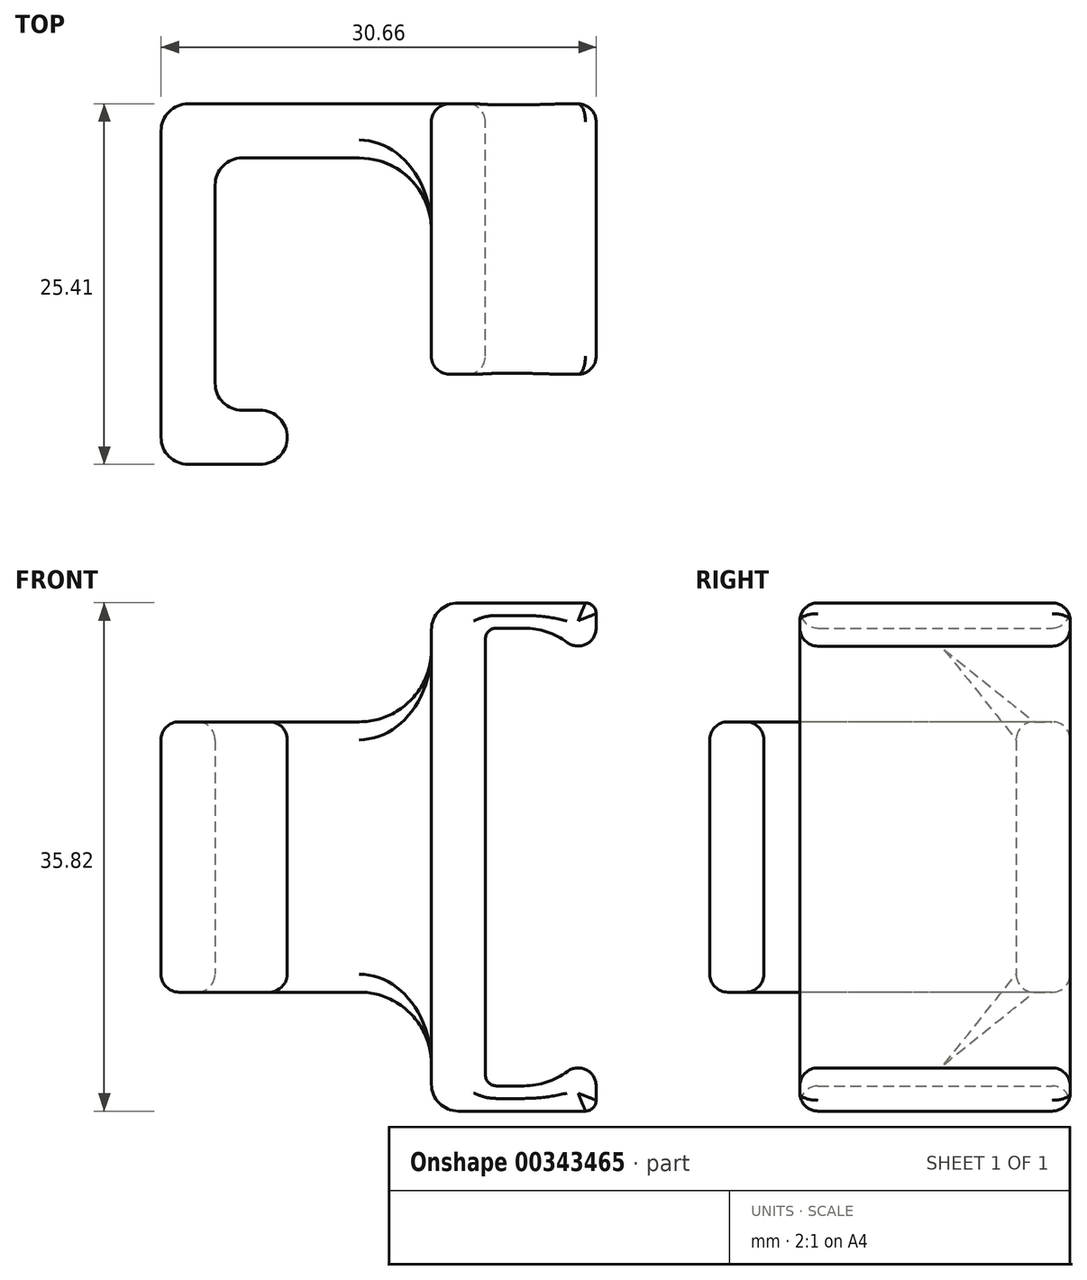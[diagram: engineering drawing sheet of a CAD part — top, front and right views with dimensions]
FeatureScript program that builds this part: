
annotation { "Feature Type Name" : "Feature", "Feature Type Description" : "" }
export const myFeature = defineFeature(function(context is Context, id is Id, definition is map)
    precondition{}
    {
        {
            var Q0;
            Q0=qCreatedBy(makeId("Front.planeOp"),FACE);
            var sketch = newSketch(context, id + "F0", { "sketchPlane" : qUnion([Q0])});
            skLineSegment(sketch, "E0.top", {"start": v(1.9, 17.9) * mm, "end": v(3.8, 17.9) * mm});
            skLineSegment(sketch, "E0.left", {"start": v(0, -16) * mm, "end": v(0, 16) * mm});
            skLineSegment(sketch, "E0.right", {"start": v(3.8, -15.37) * mm, "end": v(3.8, 15.37) * mm});
            skLineSegment(sketch, "E1", {"start": v(4.57, 16.13) * mm, "end": v(9.07, 16.13) * mm});
            skLineSegment(sketch, "E2", {"start": v(4.57, -16.13) * mm, "end": v(9.07, -16.13) * mm});
            skLineSegment(sketch, "E3", {"start": v(1.9, -17.9) * mm, "end": v(10.85, -17.9) * mm});
            skLineSegment(sketch, "E4", {"start": v(3.8, 17.9) * mm, "end": v(10.85, 17.9) * mm});
            skLineSegment(sketch, "E5.trimOffspring", {"start": v(3.8, 17.9) * mm, "end": v(3.8, 17.9) * mm});
            skLineSegment(sketch, "E6", {"start": v(11.6, -16.13) * mm, "end": v(11.6, -17.14) * mm});
            skLineSegment(sketch, "E7", {"start": v(11.6, 16.13) * mm, "end": v(11.6, 17.14) * mm});
            skPoint(sketch, "E8.visualSharp", {"position": v(0, -17.9) * mm});
            skArc(sketch, "E8.filletArc", {"start": v(0, -16) * mm, "mid": v(0.56, -17.35) * mm, "end": v(1.9, -17.9) * mm});
            skPoint(sketch, "E9.visualSharp", {"position": v(3.8, -16.13) * mm});
            skArc(sketch, "E9.filletArc", {"start": v(3.8, -15.37) * mm, "mid": v(4.03, -15.9) * mm, "end": v(4.57, -16.13) * mm});
            skPoint(sketch, "E10.visualSharp", {"position": v(3.8, 16.13) * mm});
            skArc(sketch, "E10.filletArc", {"start": v(4.57, 16.13) * mm, "mid": v(4.03, 15.9) * mm, "end": v(3.8, 15.37) * mm});
            skPoint(sketch, "E11.visualSharp", {"position": v(11.6, 17.9) * mm});
            skArc(sketch, "E11.filletArc", {"start": v(11.6, 17.14) * mm, "mid": v(11.38, 17.68) * mm, "end": v(10.85, 17.9) * mm});
            skPoint(sketch, "E12.visualSharp", {"position": v(11.6, -17.9) * mm});
            skArc(sketch, "E12.filletArc", {"start": v(10.85, -17.9) * mm, "mid": v(11.38, -17.68) * mm, "end": v(11.6, -17.14) * mm});
            skLineSegment(sketch, "E13", {"start": v(11.6, 16.13) * mm, "end": v(9.07, 16.13) * mm, "construction": true});
            skArc(sketch, "E14", {"start": v(11.6, 16.13) * mm, "mid": v(10.34, 14.86) * mm, "end": v(9.07, 16.13) * mm});
            skLineSegment(sketch, "E15", {"start": v(11.6, -16.13) * mm, "end": v(9.07, -16.13) * mm, "construction": true});
            skArc(sketch, "E16", {"start": v(11.6, -16.13) * mm, "mid": v(10.34, -14.86) * mm, "end": v(9.07, -16.13) * mm});
            skPoint(sketch, "E17.visualSharp", {"position": v(0, 17.9) * mm});
            skArc(sketch, "E17.filletArc", {"start": v(1.9, 17.9) * mm, "mid": v(0.56, 17.35) * mm, "end": v(0, 16) * mm});
            skSolve(sketch);
        }
        {
            var Q0;
            Q0 = qSketchRegion(id + "F0", true);
            extrude(context, id + "F1", {"entities" : qUnion([Q0]), "endBound" : BoundingType.SYMMETRIC, "depth" : 19.05 * mm});
        }
        {
            var Q0;
            Q0=qCreatedBy(makeId("Top.planeOp"),FACE);
            var sketch = newSketch(context, id + "F2", { "sketchPlane" : qUnion([Q0])});
            skLineSegment(sketch, "E18", {"start": v(1.9, 9.53) * mm, "end": v(-17.14, 9.52) * mm});
            skLineSegment(sketch, "E19", {"start": v(-19.05, 7.62) * mm, "end": v(-19.05, -13.97) * mm});
            skLineSegment(sketch, "E20", {"start": v(-15.24, 3.8) * mm, "end": v(-15.24, -10.16) * mm});
            skLineSegment(sketch, "E21", {"start": v(-15.24, -15.88) * mm, "end": v(-17.14, -15.88) * mm});
            skLineSegment(sketch, "E22", {"start": v(-13.33, 5.71) * mm, "end": v(1.9, 5.71) * mm});
            skLineSegment(sketch, "E23", {"start": v(-15.24, -15.88) * mm, "end": v(-12.07, -15.88) * mm});
            skLineSegment(sketch, "E24", {"start": v(-10.16, -13.97) * mm, "end": v(-10.16, -13.97) * mm});
            skLineSegment(sketch, "E25", {"start": v(-12.07, -12.07) * mm, "end": v(-13.33, -12.07) * mm});
            skPoint(sketch, "E26.visualSharp", {"position": v(-15.24, -12.07) * mm});
            skArc(sketch, "E26.filletArc", {"start": v(-15.24, -10.16) * mm, "mid": v(-14.68, -11.5) * mm, "end": v(-13.33, -12.07) * mm});
            skPoint(sketch, "E27.visualSharp", {"position": v(-19.05, -15.88) * mm});
            skArc(sketch, "E27.filletArc", {"start": v(-19.05, -13.97) * mm, "mid": v(-18.5, -15.32) * mm, "end": v(-17.14, -15.88) * mm});
            skPoint(sketch, "E28.visualSharp", {"position": v(-19.05, 9.52) * mm});
            skArc(sketch, "E28.filletArc", {"start": v(-17.14, 9.52) * mm, "mid": v(-18.5, 8.97) * mm, "end": v(-19.05, 7.62) * mm});
            skPoint(sketch, "E29.visualSharp", {"position": v(-15.24, 5.71) * mm});
            skArc(sketch, "E29.filletArc", {"start": v(-13.33, 5.72) * mm, "mid": v(-14.68, 5.16) * mm, "end": v(-15.24, 3.8) * mm});
            skPoint(sketch, "E30.visualSharp", {"position": v(-10.16, -12.07) * mm});
            skArc(sketch, "E30.filletArc", {"start": v(-10.16, -13.97) * mm, "mid": v(-10.72, -12.62) * mm, "end": v(-12.07, -12.07) * mm});
            skPoint(sketch, "E31.visualSharp", {"position": v(-10.16, -15.88) * mm});
            skArc(sketch, "E31.filletArc", {"start": v(-12.07, -15.88) * mm, "mid": v(-10.72, -15.32) * mm, "end": v(-10.16, -13.97) * mm});
            skLineSegment(sketch, "E32", {"start": v(1.9, 9.53) * mm, "end": v(1.9, 5.71) * mm});
            skPoint(sketch, "E33.orphan", {"position": v(1.26, 5.71) * mm});
            skSolve(sketch);
        }
        {
            var Q0;
            Q0 = qSketchRegion(id + "F2", true);
            extrude(context, id + "F3", {"entities" : qUnion([Q0]), "operationType" : NewBodyOperationType.ADD, "endBound" : BoundingType.SYMMETRIC, "depth" : 19.05 * mm});
        }
        {
            var Q0;
            Q0=makeQuery(id+"F1.opExtrude","SWEPT_EDGE",EDGE,{"disambiguationData":[OSD([sQuery(id+"F0.wireOp",EDGE,"E1"),sQuery(id+"F0.wireOp",EDGE,"E14")])]});
            var Q1;
            Q1=makeQuery(id+"F1.opExtrude","SWEPT_EDGE",EDGE,{"disambiguationData":[OSD([sQuery(id+"F0.wireOp",EDGE,"E2"),sQuery(id+"F0.wireOp",EDGE,"E16")])]});
            var Q2;
            Q2=makeQuery(id+"F3.boolean.opBoolean","INTERSECT",EDGE,{"derivedFrom":[makeQuery(id+"F1.opExtrude","SWEPT_FACE",FACE,{"disambiguationData":[OSD([sQuery(id+"F0.wireOp",EDGE,"E0.left")])]}),makeQuery(id+"F3.opExtrude","SWEPT_FACE",FACE,{"disambiguationData":[OSD([sQuery(id+"F2.wireOp",EDGE,"E22")])]})]});
            var Q3;
            Q3=makeQuery(id+"F3.boolean.opBoolean","INTERSECT",EDGE,{"derivedFrom":[makeQuery(id+"F1.opExtrude","SWEPT_FACE",FACE,{"disambiguationData":[OSD([sQuery(id+"F0.wireOp",EDGE,"E0.left")])]}),makeQuery(id+"F3.opExtrude","CAP_FACE",FACE,{"disambiguationData":[OSD([sQuery(id+"F2.wireOp",EDGE,"E18"),sQuery(id+"F2.wireOp",EDGE,"E19"),sQuery(id+"F2.wireOp",EDGE,"E20"),sQuery(id+"F2.wireOp",EDGE,"E21"),sQuery(id+"F2.wireOp",EDGE,"E22"),sQuery(id+"F2.wireOp",EDGE,"E23"),sQuery(id+"F2.wireOp",EDGE,"E25"),sQuery(id+"F2.wireOp",EDGE,"E26.filletArc"),sQuery(id+"F2.wireOp",EDGE,"E27.filletArc"),sQuery(id+"F2.wireOp",EDGE,"E28.filletArc"),sQuery(id+"F2.wireOp",EDGE,"E29.filletArc"),sQuery(id+"F2.wireOp",EDGE,"E30.filletArc"),sQuery(id+"F2.wireOp",EDGE,"E31.filletArc"),sQuery(id+"F2.wireOp",EDGE,"E32")])],"isStart":false})]});
            var Q4;
            Q4=makeQuery(id+"F3.boolean.opBoolean","INTERSECT",EDGE,{"derivedFrom":[makeQuery(id+"F1.opExtrude","SWEPT_FACE",FACE,{"disambiguationData":[OSD([sQuery(id+"F0.wireOp",EDGE,"E0.left")])]}),makeQuery(id+"F3.opExtrude","CAP_FACE",FACE,{"disambiguationData":[OSD([sQuery(id+"F2.wireOp",EDGE,"E18"),sQuery(id+"F2.wireOp",EDGE,"E19"),sQuery(id+"F2.wireOp",EDGE,"E20"),sQuery(id+"F2.wireOp",EDGE,"E21"),sQuery(id+"F2.wireOp",EDGE,"E22"),sQuery(id+"F2.wireOp",EDGE,"E23"),sQuery(id+"F2.wireOp",EDGE,"E25"),sQuery(id+"F2.wireOp",EDGE,"E26.filletArc"),sQuery(id+"F2.wireOp",EDGE,"E27.filletArc"),sQuery(id+"F2.wireOp",EDGE,"E28.filletArc"),sQuery(id+"F2.wireOp",EDGE,"E29.filletArc"),sQuery(id+"F2.wireOp",EDGE,"E30.filletArc"),sQuery(id+"F2.wireOp",EDGE,"E31.filletArc"),sQuery(id+"F2.wireOp",EDGE,"E32")])],"isStart":true})]});
            fillet(context, id + "F4", {"entities" : qUnion([Q0, Q1, Q2, Q3, Q4]), "radius" : 5.08 * mm, "tangentPropagation" : true, "allowEdgeOverflow" : false});
        }
        {
            var Q0;
            Q0=makeQuery(id+"F3.opExtrude","CAP_EDGE",EDGE,{"disambiguationData":[OSD([sQuery(id+"F2.wireOp",EDGE,"E20")])],"isStart":false});
            var Q1;
            Q1=makeQuery(id+"F1.opExtrude","CAP_EDGE",EDGE,{"disambiguationData":[OSD([sQuery(id+"F0.wireOp",EDGE,"E0.left")])],"isStart":false});
            fillet(context, id + "F5", {"entities" : qUnion([Q0, Q1]), "radius" : 1.27 * mm, "tangentPropagation" : true, "allowEdgeOverflow" : false});
        }
    });
